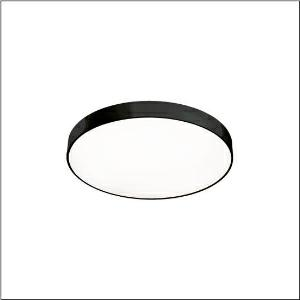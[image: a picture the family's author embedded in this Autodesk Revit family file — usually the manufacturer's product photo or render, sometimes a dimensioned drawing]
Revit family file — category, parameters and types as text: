
# Revit family: round_21_m_51mr36fd0421b
name_source: partatom
category: Lighting Fixtures
units: mm (PartAtom-declared; Revit-internal decimal feet)

## family parameters
Cut with Voids When Loaded = No
Host = Face
Light Source = No
Part Type = Normal
Room Calculation Point = No
Round Connector Dimension = Use Diameter
Shared = No

## types (1)
- Round 21 M (1 x LED, 7810 lm, 54.9 W, 4000K)
    Apparent Load = 55 VA
    CIE Flux Codes = 49 80 96 100 100
    Color Rendering = 80
    Color Temperature = 4000K
    Default Elevation = 1800 mm
    Description = Round 21 M, wall and ceiling luminaire, primary optical cover: cover, of PMMA, opal, light emission: direct distribution, primary light characteristic: symmetric, installation type: surface-mounted, suspended mounting, LED, rated luminous flux: 7.810lm, luminous efficacy: 142lm/W, light colour: 840, colour temperature: 4000K, control gear: DALI 2, with terminal, 5-pole, mains connection: 230V, AC, 50/60Hz, rated input power: 55W, housing, of aluminium, coated, black, diameter: 600mm, height: 62mm, protection rating (complete): IP40, insulation class (complete): insulation class I (protective earthing), certification: CE, impact resistance: IK04, permissible operating ambient temperature: -10..+35°C, packaging unit: 1 piece
    Height = 87 mm
    Lamp = 1 x LED
    Lamp Light Flux = 7810 lm
    Lamp Power = 54.9 W
    Lamp count = 1
    Length = 600 mm
    Luminous efficacy = 142 lm/W
    Manufacturer = Siteco
    ModVariant = No
    Model = 51MR36FD0421B
    Mounting Place = Ceiling
    Mounting Type = Surface mounted
    Number of Poles = 1
    OnlyDefault = Yes
    Power Factor = 1
    Product Name = Round 21 M
    Product group = wall and ceiling luminaire | ceiling mounted
    ProductGroupID = 304
    Protection Class = Protection class I
    Protection Degree = IP 40
    RLX_Detail_Level = 1
    RLX_Emergency_Light_Flux = 0 lm
    RLX_Emergency_Type = 0
    RLX_Emergency_Type_DB = No
    RlxData = <blob elided: 17753 chars, md5=16bd9cc1>
    Socket = socket
    Standby Power = 0 W
    System Light Flux = 7810 lm
    System Power = 55 W
    Type Comments = Product without accessories
    Type Image = l_1258332.jpg
    URL = http://relux.com
    VarID = ---
    Voltage = 0 V
    Weight = 0.00 kg
    Width = 0 mm  [stored 0 ft]

note: [stored X ft] marks values corroborated as IEEE doubles in the binary element streams (Revit-internal decimal feet)

## geometry (parser evidence)
native form markers: Blend x4, Sweep x10
no freeform markers — native parametric forms only
